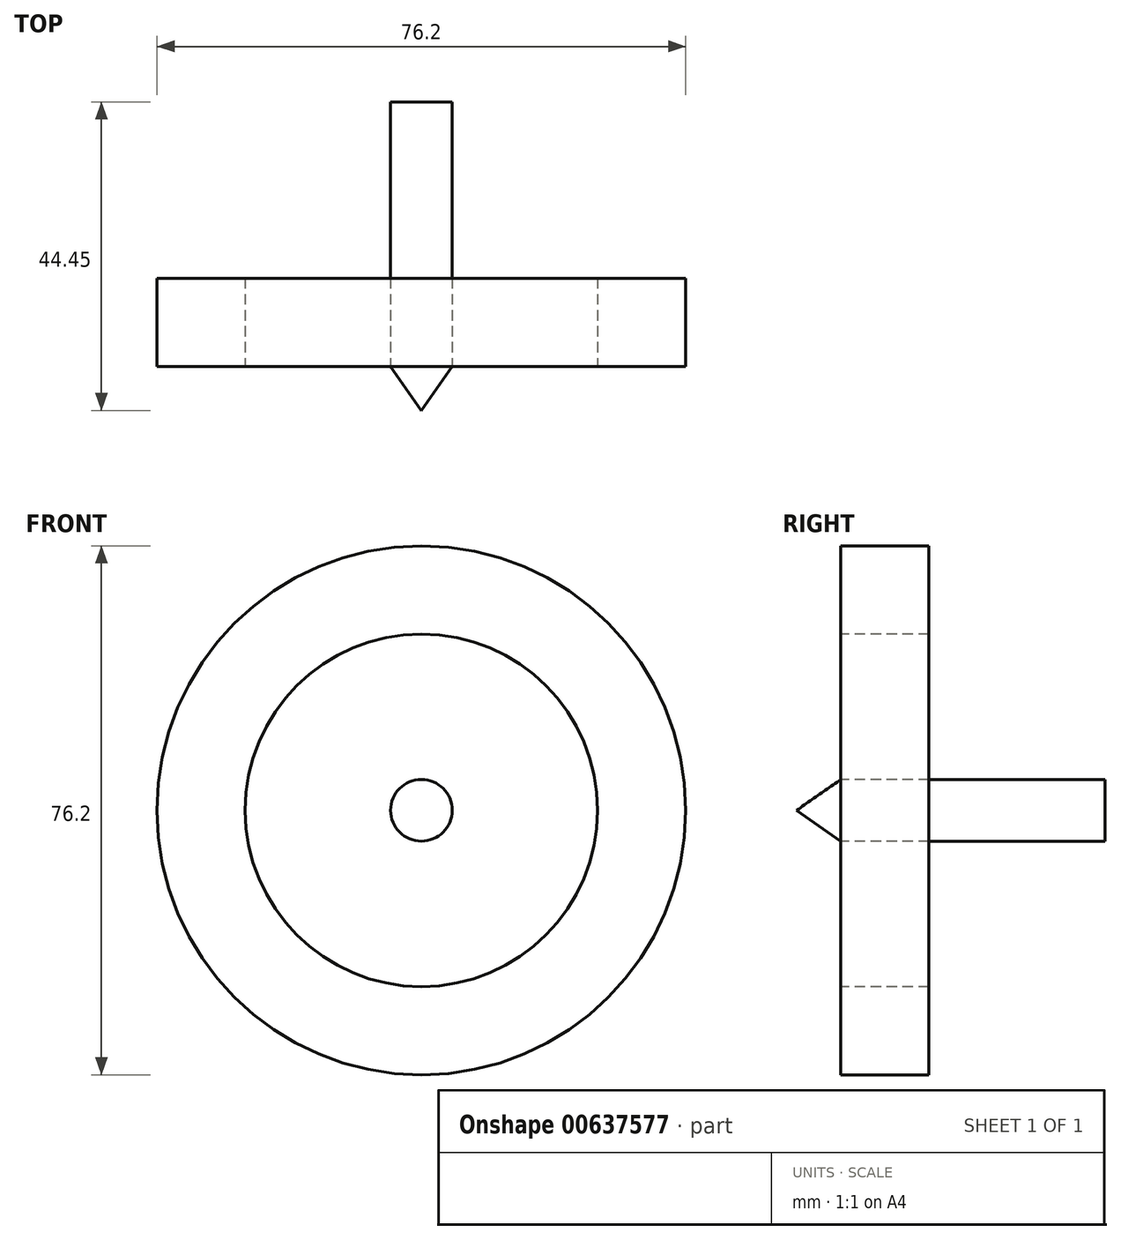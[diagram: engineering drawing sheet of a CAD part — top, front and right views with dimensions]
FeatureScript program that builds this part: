
annotation { "Feature Type Name" : "Feature", "Feature Type Description" : "" }
export const myFeature = defineFeature(function(context is Context, id is Id, definition is map)
    precondition{}
    {
        {
            var Q0;
            Q0=qCreatedBy(makeId("Top.planeOp"),FACE);
            var sketch = newSketch(context, id + "F0", { "sketchPlane" : qUnion([Q0])});
            skLineSegment(sketch, "E0.bottom", {"start": v(25.4, 0) * mm, "end": v(38.1, 0) * mm});
            skLineSegment(sketch, "E0.top", {"start": v(25.4, 12.7) * mm, "end": v(38.1, 12.7) * mm});
            skLineSegment(sketch, "E0.left", {"start": v(25.4, 0) * mm, "end": v(25.4, 12.7) * mm});
            skLineSegment(sketch, "E0.right", {"start": v(38.1, 0) * mm, "end": v(38.1, 12.7) * mm});
            skLineSegment(sketch, "E1", {"start": v(0, 0) * mm, "end": v(0, 54.93) * mm, "construction": true});
            skSolve(sketch);
        }
        {
            var Q0;
            Q0=makeQuery(id+"F0.imprint","IMPRINT",FACE,{"disambiguationData":[TD([[makeQuery(id+"F0.imprint","IMPRINT",EDGE,{"derivedFrom":sQuery(id+"F0.wireOp",EDGE,"E0.bottom")}),1.0]])]});
            var Q1;
            Q1=sQuery(id+"F0.wireOp",EDGE,"E1");
            revolve(context, id + "F1", {"entities" : qUnion([Q0]), "axis" : qUnion([Q1]), "revolveType" : RevolveType.FULL});
        }
        {
            var Q0;
            Q0=qCreatedBy(makeId("Front.planeOp"),FACE);
            var sketch = newSketch(context, id + "F2", { "sketchPlane" : qUnion([Q0])});
            skCircle(sketch, "E2", {"center": v(0, 0) * mm, "radius": 4.44 * mm});
            skSolve(sketch);
        }
        {
            var Q0;
            Q0=makeQuery(id+"F2.imprint","IMPRINT",FACE,{"disambiguationData":[TD([[makeQuery(id+"F2.imprint","IMPRINT",EDGE,{"derivedFrom":sQuery(id+"F2.wireOp",EDGE,"E2")}),1.0]])]});
            extrude(context, id + "F3", {"entities" : qUnion([Q0]), "depth" : -38.1 * mm, "offsetDistance" : 25.4 * mm});
        }
        {
            var Q0;
            Q0=qCreatedBy(makeId("Right.planeOp"),FACE);
            var sketch = newSketch(context, id + "F4", { "sketchPlane" : qUnion([Q0])});
            skLineSegment(sketch, "E3", {"start": v(0, 0) * mm, "end": v(0, 4.45) * mm});
            skLineSegment(sketch, "E4", {"start": v(0, 0) * mm, "end": v(-6.35, 0) * mm});
            skLineSegment(sketch, "E5", {"start": v(-6.35, 0) * mm, "end": v(0, 4.44) * mm});
            skLineSegment(sketch, "E6", {"start": v(0, 0) * mm, "end": v(-43.34, 0) * mm, "construction": true});
            skSolve(sketch);
        }
        {
            var Q0;
            Q0=makeQuery(id+"F4.imprint","IMPRINT",FACE,{"disambiguationData":[TD([[makeQuery(id+"F4.imprint","IMPRINT",EDGE,{"derivedFrom":sQuery(id+"F4.wireOp",EDGE,"E3")}),1.0]])]});
            var Q1;
            Q1=sQuery(id+"F4.wireOp",EDGE,"E6");
            revolve(context, id + "F5", {"operationType" : NewBodyOperationType.ADD, "entities" : qUnion([Q0]), "axis" : qUnion([Q1]), "revolveType" : RevolveType.FULL});
        }
    });
